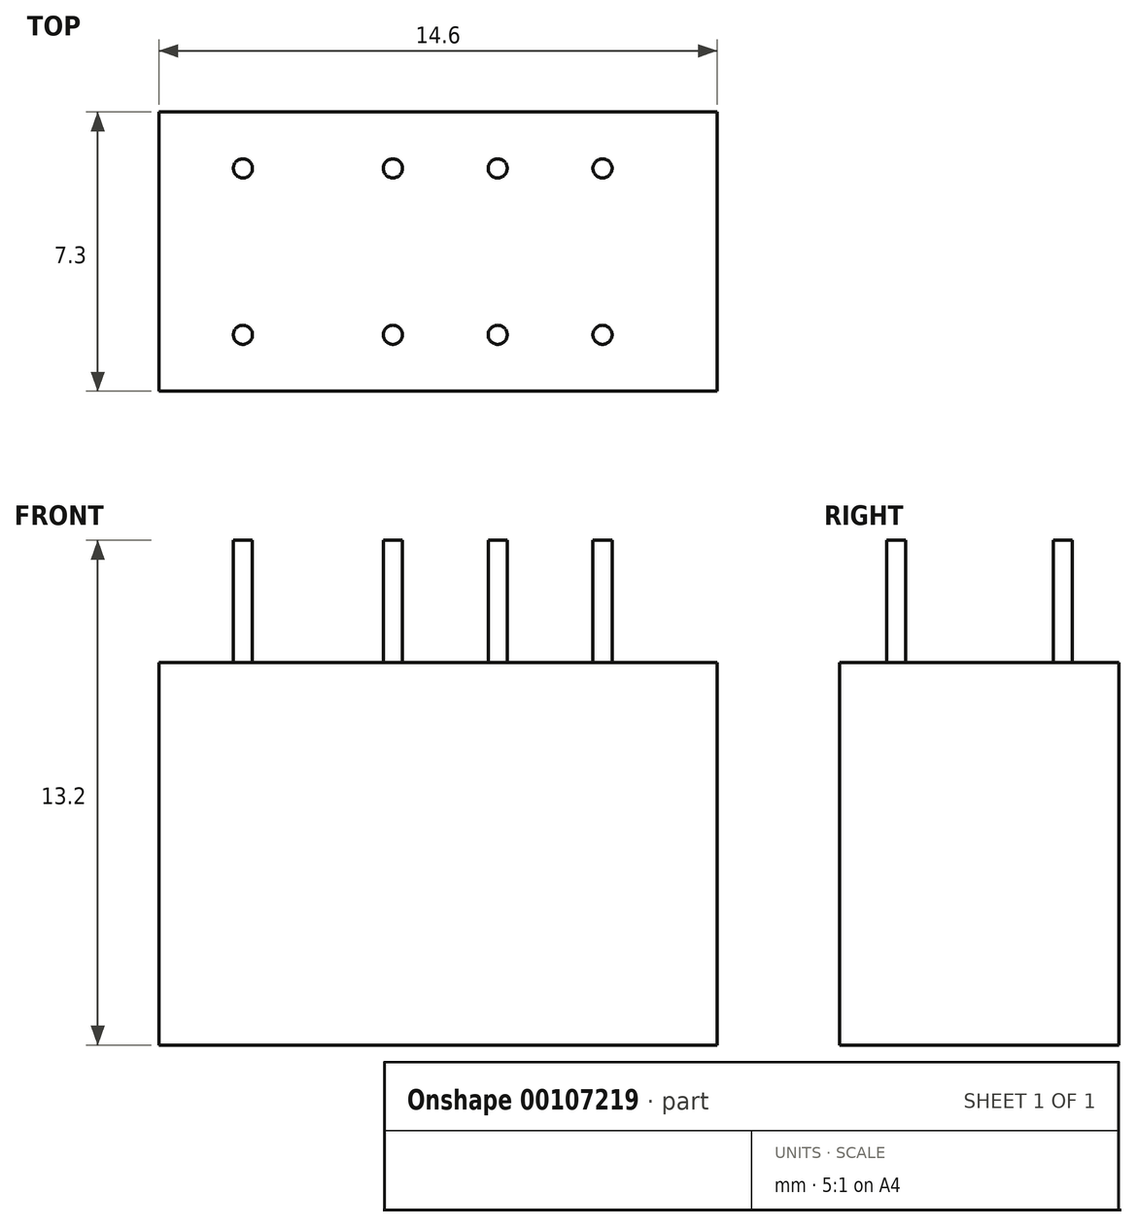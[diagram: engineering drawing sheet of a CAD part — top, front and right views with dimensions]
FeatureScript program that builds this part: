
annotation { "Feature Type Name" : "Feature", "Feature Type Description" : "" }
export const myFeature = defineFeature(function(context is Context, id is Id, definition is map)
    precondition{}
    {
        {
            var Q0;
            Q0=qCreatedBy(makeId("Top.planeOp"),FACE);
            var sketch = newSketch(context, id + "F0", { "sketchPlane" : qUnion([Q0])});
            skLineSegment(sketch, "E0.bottom", {"start": v(0, 0) * mm, "end": v(14.6, 0) * mm});
            skLineSegment(sketch, "E0.top", {"start": v(0, 7.3) * mm, "end": v(14.6, 7.3) * mm});
            skLineSegment(sketch, "E0.left", {"start": v(0, 0) * mm, "end": v(0, 7.3) * mm});
            skLineSegment(sketch, "E0.right", {"start": v(14.6, 0) * mm, "end": v(14.6, 7.3) * mm});
            skSolve(sketch);
        }
        {
            var Q0;
            Q0=makeQuery(id+"F0.imprint","IMPRINT",FACE,{"disambiguationData":[TD([[makeQuery(id+"F0.imprint","IMPRINT",EDGE,{"derivedFrom":sQuery(id+"F0.wireOp",EDGE,"E0.bottom")}),1.0]])]});
            extrude(context, id + "F1", {"entities" : qUnion([Q0]), "depth" : 10 * mm});
        }
        {
            var Q0;
            Q0=makeQuery(id+"F1.opExtrude","CAP_FACE",FACE,{"disambiguationData":[OSD([sQuery(id+"F0.wireOp",EDGE,"E0.bottom"),sQuery(id+"F0.wireOp",EDGE,"E0.top"),sQuery(id+"F0.wireOp",EDGE,"E0.left"),sQuery(id+"F0.wireOp",EDGE,"E0.right")])],"isStart":false});
            var sketch = newSketch(context, id + "F2", { "sketchPlane" : qUnion([Q0])});
            skCircle(sketch, "E1", {"center": v(2.2, 5.83) * mm, "radius": 0.25 * mm});
            skCircle(sketch, "E2", {"center": v(6.12, 5.83) * mm, "radius": 0.25 * mm});
            skCircle(sketch, "E3", {"center": v(8.86, 5.83) * mm, "radius": 0.25 * mm});
            skCircle(sketch, "E4", {"center": v(11.6, 5.83) * mm, "radius": 0.25 * mm});
            skCircle(sketch, "E5", {"center": v(6.12, 1.47) * mm, "radius": 0.25 * mm});
            skCircle(sketch, "E6", {"center": v(8.86, 1.47) * mm, "radius": 0.25 * mm});
            skCircle(sketch, "E7", {"center": v(11.6, 1.47) * mm, "radius": 0.25 * mm});
            skCircle(sketch, "E8", {"center": v(2.2, 1.47) * mm, "radius": 0.25 * mm});
            skLineSegment(sketch, "E9", {"start": v(2.2, 5.83) * mm, "end": v(11.6, 5.83) * mm, "construction": true});
            skLineSegment(sketch, "E10", {"start": v(2.2, 1.47) * mm, "end": v(11.6, 1.47) * mm, "construction": true});
            skLineSegment(sketch, "E11", {"start": v(6.12, 5.83) * mm, "end": v(6.12, 1.47) * mm, "construction": true});
            skLineSegment(sketch, "E12", {"start": v(8.86, 1.47) * mm, "end": v(8.86, 5.83) * mm, "construction": true});
            skLineSegment(sketch, "E13", {"start": v(11.6, 5.83) * mm, "end": v(11.6, 1.47) * mm, "construction": true});
            skLineSegment(sketch, "E14", {"start": v(2.2, 5.83) * mm, "end": v(2.2, 1.47) * mm, "construction": true});
            skLineSegment(sketch, "E15", {"start": v(2.2, 3.65) * mm, "end": v(0, 3.65) * mm, "construction": true});
            skSolve(sketch);
        }
        {
            var Q0;
            Q0=makeQuery(id+"F2.imprint","IMPRINT",FACE,{"disambiguationData":[TD([[makeQuery(id+"F2.imprint","IMPRINT",EDGE,{"derivedFrom":sQuery(id+"F2.wireOp",EDGE,"E1")}),1.0]])]});
            var Q1;
            Q1=makeQuery(id+"F2.imprint","IMPRINT",FACE,{"disambiguationData":[TD([[makeQuery(id+"F2.imprint","IMPRINT",EDGE,{"derivedFrom":sQuery(id+"F2.wireOp",EDGE,"E8")}),1.0]])]});
            var Q2;
            Q2=makeQuery(id+"F2.imprint","IMPRINT",FACE,{"disambiguationData":[TD([[makeQuery(id+"F2.imprint","IMPRINT",EDGE,{"derivedFrom":sQuery(id+"F2.wireOp",EDGE,"E5")}),1.0]])]});
            var Q3;
            Q3=makeQuery(id+"F2.imprint","IMPRINT",FACE,{"disambiguationData":[TD([[makeQuery(id+"F2.imprint","IMPRINT",EDGE,{"derivedFrom":sQuery(id+"F2.wireOp",EDGE,"E2")}),1.0]])]});
            var Q4;
            Q4=makeQuery(id+"F2.imprint","IMPRINT",FACE,{"disambiguationData":[TD([[makeQuery(id+"F2.imprint","IMPRINT",EDGE,{"derivedFrom":sQuery(id+"F2.wireOp",EDGE,"E3")}),1.0]])]});
            var Q5;
            Q5=makeQuery(id+"F2.imprint","IMPRINT",FACE,{"disambiguationData":[TD([[makeQuery(id+"F2.imprint","IMPRINT",EDGE,{"derivedFrom":sQuery(id+"F2.wireOp",EDGE,"E4")}),1.0]])]});
            var Q6;
            Q6=makeQuery(id+"F2.imprint","IMPRINT",FACE,{"disambiguationData":[TD([[makeQuery(id+"F2.imprint","IMPRINT",EDGE,{"derivedFrom":sQuery(id+"F2.wireOp",EDGE,"E7")}),1.0]])]});
            var Q7;
            Q7=makeQuery(id+"F2.imprint","IMPRINT",FACE,{"disambiguationData":[TD([[makeQuery(id+"F2.imprint","IMPRINT",EDGE,{"derivedFrom":sQuery(id+"F2.wireOp",EDGE,"E6")}),1.0]])]});
            extrude(context, id + "F3", {"entities" : qUnion([Q0, Q1, Q2, Q3, Q4, Q5, Q6, Q7]), "operationType" : NewBodyOperationType.ADD, "depth" : 3.2 * mm});
        }
    });
